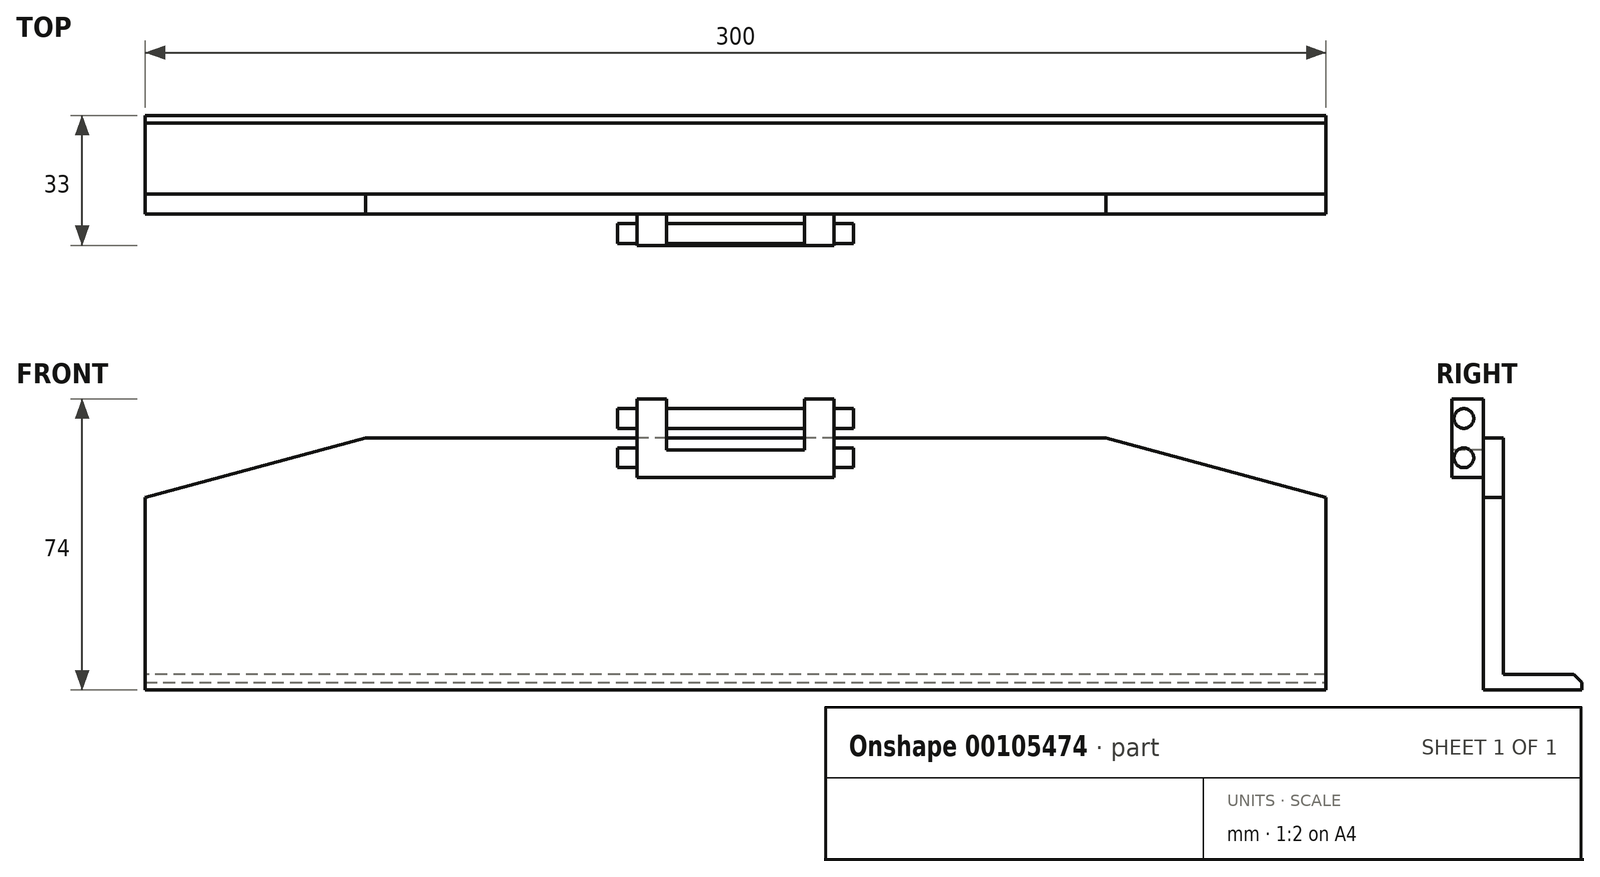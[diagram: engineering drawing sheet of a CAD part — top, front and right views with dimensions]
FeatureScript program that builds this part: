
annotation { "Feature Type Name" : "Feature", "Feature Type Description" : "" }
export const myFeature = defineFeature(function(context is Context, id is Id, definition is map)
    precondition{}
    {
        {
            var Q0;
            Q0=qCreatedBy(makeId("Top.planeOp"),FACE);
            var sketch = newSketch(context, id + "F0", { "sketchPlane" : qUnion([Q0])});
            skLineSegment(sketch, "E0.bottom", {"start": v(150, -12.5) * mm, "end": v(-150, -12.5) * mm});
            skLineSegment(sketch, "E0.top", {"start": v(150, 12.5) * mm, "end": v(-150, 12.5) * mm});
            skLineSegment(sketch, "E0.left", {"start": v(150, -12.5) * mm, "end": v(150, 12.5) * mm});
            skLineSegment(sketch, "E0.right", {"start": v(-150, -12.5) * mm, "end": v(-150, 12.5) * mm});
            skPoint(sketch, "E0.middle", {"position": v(0, 0) * mm});
            skSolve(sketch);
        }
        {
            var Q0;
            Q0=makeQuery(id+"F0.imprint","IMPRINT",FACE,{"disambiguationData":[TD([[makeQuery(id+"F0.imprint","IMPRINT",EDGE,{"derivedFrom":sQuery(id+"F0.wireOp",EDGE,"E0.bottom")}),-1.0]])]});
            extrude(context, id + "F1", {"entities" : qUnion([Q0]), "depth" : 4 * mm});
        }
        {
            var Q0;
            Q0=makeQuery(id+"F1.opExtrude","CAP_FACE",FACE,{"disambiguationData":[OSD([sQuery(id+"F0.wireOp",EDGE,"E0.bottom"),sQuery(id+"F0.wireOp",EDGE,"E0.top"),sQuery(id+"F0.wireOp",EDGE,"E0.left"),sQuery(id+"F0.wireOp",EDGE,"E0.right")])],"isStart":false});
            var sketch = newSketch(context, id + "F2", { "sketchPlane" : qUnion([Q0])});
            skLineSegment(sketch, "E1.bottom", {"start": v(-150, -12.5) * mm, "end": v(150, -12.5) * mm});
            skLineSegment(sketch, "E1.top", {"start": v(-150, -7.5) * mm, "end": v(150, -7.5) * mm});
            skLineSegment(sketch, "E1.left", {"start": v(-150, -12.5) * mm, "end": v(-150, -7.5) * mm});
            skLineSegment(sketch, "E1.right", {"start": v(150, -12.5) * mm, "end": v(150, -7.5) * mm});
            skSolve(sketch);
        }
        {
            var Q0;
            Q0 = qSketchRegion(id + "F2", true);
            extrude(context, id + "F3", {"entities" : qUnion([Q0]), "operationType" : NewBodyOperationType.ADD, "depth" : 60 * mm});
        }
        {
            var Q0;
            Q0=makeQuery(id+"F3.opExtrude","CAP_EDGE",EDGE,{"disambiguationData":[OSD([sQuery(id+"F2.wireOp",EDGE,"E1.left")])],"isStart":false});
            var Q1;
            Q1=makeQuery(id+"F3.opExtrude","CAP_EDGE",EDGE,{"disambiguationData":[OSD([sQuery(id+"F2.wireOp",EDGE,"E1.right")])],"isStart":false});
            chamfer(context, id + "F4", {"entities" : qUnion([Q0, Q1]), "chamferType" : ChamferType.OFFSET_ANGLE, "width" : 15 * mm, "oppositeDirection" : false, "angle" : 75 * degree, "tangentPropagation" : true});
        }
        {
            var Q0;
            Q0=makeQuery(id+"F1.opExtrude","CAP_EDGE",EDGE,{"disambiguationData":[OSD([sQuery(id+"F0.wireOp",EDGE,"E0.top")])],"isStart":false});
            chamfer(context, id + "F5", {"entities" : qUnion([Q0]), "width" : 2 * mm, "tangentPropagation" : true});
        }
        {
            var Q0;
            Q0=makeQuery(id+"F3.boolean.opBoolean","MERGE",FACE,{"derivedFrom":[makeQuery(id+"F1.opExtrude","SWEPT_FACE",FACE,{"disambiguationData":[OSD([sQuery(id+"F0.wireOp",EDGE,"E0.bottom")])]}),makeQuery(id+"F3.opExtrude","SWEPT_FACE",FACE,{"disambiguationData":[OSD([sQuery(id+"F2.wireOp",EDGE,"E1.bottom")])]})]});
            var sketch = newSketch(context, id + "F6", { "sketchPlane" : qUnion([Q0])});
            skLineSegment(sketch, "E2.bottom", {"start": v(25, 74) * mm, "end": v(-25, 74) * mm});
            skLineSegment(sketch, "E2.top", {"start": v(25, 54) * mm, "end": v(-25, 54) * mm});
            skLineSegment(sketch, "E2.left", {"start": v(25, 74) * mm, "end": v(25, 54) * mm});
            skLineSegment(sketch, "E2.right", {"start": v(-25, 74) * mm, "end": v(-25, 54) * mm});
            skPoint(sketch, "E2.middle", {"position": v(0, 64) * mm});
            skSolve(sketch);
        }
        {
            var Q0;
            Q0 = qSketchRegion(id + "F6", true);
            extrude(context, id + "F7", {"entities" : qUnion([Q0]), "operationType" : NewBodyOperationType.ADD, "depth" : 8 * mm});
        }
        {
            var Q0;
            Q0=makeQuery(id+"F7.opExtrude","CAP_FACE",FACE,{"disambiguationData":[OSD([sQuery(id+"F6.wireOp",EDGE,"E2.bottom"),sQuery(id+"F6.wireOp",EDGE,"E2.top"),sQuery(id+"F6.wireOp",EDGE,"E2.left"),sQuery(id+"F6.wireOp",EDGE,"E2.right")])],"isStart":false});
            var sketch = newSketch(context, id + "F8", { "sketchPlane" : qUnion([Q0])});
            skLineSegment(sketch, "E3.bottom", {"start": v(-10, 18.71) * mm, "end": v(10, 18.71) * mm});
            skLineSegment(sketch, "E3.top", {"start": v(-10, 15.71) * mm, "end": v(10, 15.71) * mm});
            skLineSegment(sketch, "E3.left", {"start": v(-10, 18.71) * mm, "end": v(-10, 15.71) * mm});
            skLineSegment(sketch, "E3.right", {"start": v(10, 18.71) * mm, "end": v(10, 15.71) * mm});
            skPoint(sketch, "E3.middle", {"position": v(0, 17.21) * mm});
            skSolve(sketch);
        }
        {
            var Q0;
            Q0=makeQuery(id+"F7.opExtrude","SWEPT_FACE",FACE,{"disambiguationData":[OSD([sQuery(id+"F6.wireOp",EDGE,"E2.right")])]});
            var sketch = newSketch(context, id + "F9", { "sketchPlane" : qUnion([Q0])});
            skPoint(sketch, "E4.centerSnap0", {"position": v(16.5, 74) * mm});
            skPoint(sketch, "E5.centerSnap0", {"position": v(16.5, 54) * mm});
            skCircle(sketch, "E6", {"center": v(17.5, 69) * mm, "radius": 2.5 * mm});
            skCircle(sketch, "E7", {"center": v(17.5, 59) * mm, "radius": 2.5 * mm});
            skSolve(sketch);
        }
        {
            var Q0;
            Q0 = qSketchRegion(id + "F9", true);
            extrude(context, id + "F10", {"entities" : qUnion([Q0]), "operationType" : NewBodyOperationType.ADD, "depth" : 5 * mm});
        }
        {
            var Q0;
            Q0=makeQuery(id+"F7.opExtrude","SWEPT_FACE",FACE,{"disambiguationData":[OSD([sQuery(id+"F6.wireOp",EDGE,"E2.left")])]});
            var sketch = newSketch(context, id + "F11", { "sketchPlane" : qUnion([Q0])});
            skPoint(sketch, "E8.centerSnap0", {"position": v(-16.5, 74) * mm});
            skPoint(sketch, "E9.centerSnap0", {"position": v(-16.5, 54) * mm});
            skCircle(sketch, "E10", {"center": v(-17.5, 59) * mm, "radius": 2.5 * mm});
            skCircle(sketch, "E11", {"center": v(-17.5, 69) * mm, "radius": 2.5 * mm});
            skSolve(sketch);
        }
        {
            var Q0;
            Q0 = qSketchRegion(id + "F11", true);
            extrude(context, id + "F12", {"entities" : qUnion([Q0]), "operationType" : NewBodyOperationType.ADD, "depth" : 5 * mm});
        }
        {
            var Q0;
            Q0=makeQuery(id+"F8.imprint","IMPRINT",FACE,{"disambiguationData":[TD([[makeQuery(id+"F8.imprint","IMPRINT",EDGE,{"derivedFrom":makeQuery(id+"F7.opExtrude","CAP_EDGE",EDGE,{"disambiguationData":[OSD([sQuery(id+"F6.wireOp",EDGE,"E2.bottom")])],"isStart":false})}),1.0]])]});
            var sketch = newSketch(context, id + "F13", { "sketchPlane" : qUnion([Q0])});
            skLineSegment(sketch, "E12.bottom", {"start": v(17.5, 61) * mm, "end": v(-17.5, 61) * mm});
            skLineSegment(sketch, "E12.top", {"start": v(17.5, 86) * mm, "end": v(-17.5, 86) * mm});
            skLineSegment(sketch, "E12.left", {"start": v(17.5, 61) * mm, "end": v(17.5, 86) * mm});
            skLineSegment(sketch, "E12.right", {"start": v(-17.5, 61) * mm, "end": v(-17.5, 86) * mm});
            skPoint(sketch, "E12.middle", {"position": v(0, 73.5) * mm});
            skSolve(sketch);
        }
        {
            var Q0;
            Q0 = qSketchRegion(id + "F13", true);
            extrude(context, id + "F14", {"entities" : qUnion([Q0]), "operationType" : NewBodyOperationType.REMOVE, "oppositeDirection" : true, "depth" : 8 * mm});
        }
        {
            var Q0;
            Q0=makeQuery(id+"F14.boolean.opBoolean","COPY",FACE,{"derivedFrom":makeQuery(id+"F14.opExtrude","SWEPT_FACE",FACE,{"disambiguationData":[OSD([sQuery(id+"F13.wireOp",EDGE,"E12.left")])]})});
            var sketch = newSketch(context, id + "F15", { "sketchPlane" : qUnion([Q0])});
            skCircle(sketch, "E13", {"center": v(17.5, 69) * mm, "radius": 2.5 * mm});
            skSolve(sketch);
        }
        {
            var Q0;
            Q0 = qSketchRegion(id + "F15", true);
            var Q1;
            Q1=makeQuery(id+"F14.boolean.opBoolean","COPY",FACE,{"derivedFrom":makeQuery(id+"F14.opExtrude","SWEPT_FACE",FACE,{"disambiguationData":[OSD([sQuery(id+"F13.wireOp",EDGE,"E12.right")])]})});
            extrude(context, id + "F16", {"entities" : qUnion([Q0]), "operationType" : NewBodyOperationType.ADD, "endBound" : BoundingType.UP_TO_SURFACE, "endBoundEntityFace" : qUnion([Q1]), "depth" : 25 * mm});
        }
    });
